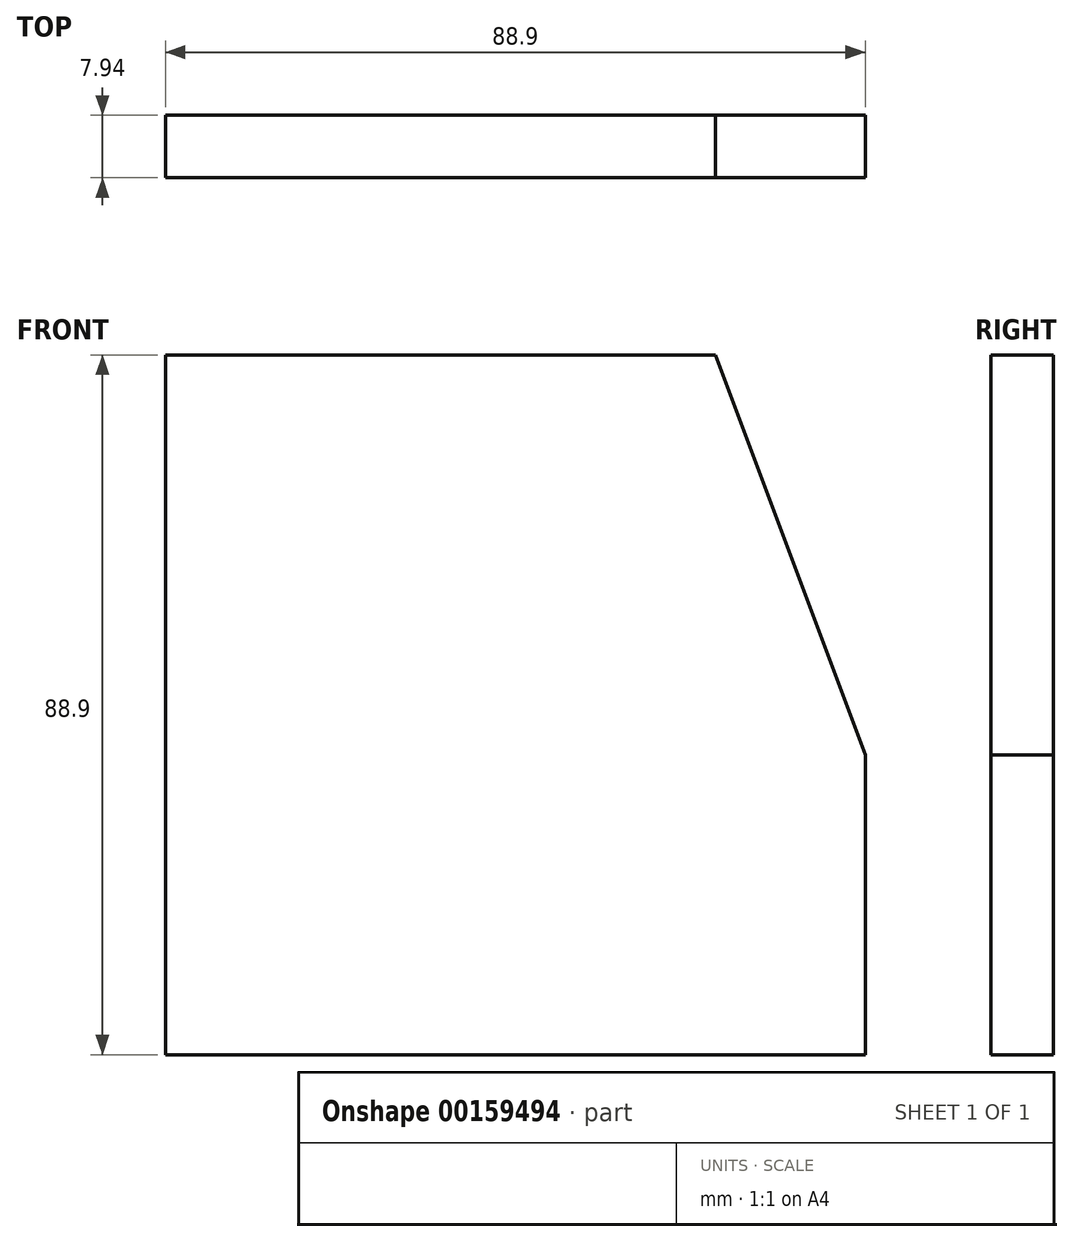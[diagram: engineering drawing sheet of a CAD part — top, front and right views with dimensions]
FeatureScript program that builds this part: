
annotation { "Feature Type Name" : "Feature", "Feature Type Description" : "" }
export const myFeature = defineFeature(function(context is Context, id is Id, definition is map)
    precondition{}
    {
        {
            var Q0;
            Q0=qCreatedBy(makeId("Front.planeOp"),FACE);
            var sketch = newSketch(context, id + "F0", { "sketchPlane" : qUnion([Q0])});
            skLineSegment(sketch, "E0.bottom", {"start": v(-78.75, 134.89) * mm, "end": v(-8.9, 134.89) * mm});
            skLineSegment(sketch, "E0.top", {"start": v(-78.75, 45.99) * mm, "end": v(10.15, 45.99) * mm});
            skLineSegment(sketch, "E0.left", {"start": v(-78.75, 134.89) * mm, "end": v(-78.75, 45.99) * mm});
            skLineSegment(sketch, "E0.right", {"start": v(10.15, 84.09) * mm, "end": v(10.15, 45.99) * mm});
            skLineSegment(sketch, "E1", {"start": v(10.15, 84.09) * mm, "end": v(-8.9, 134.89) * mm});
            skSolve(sketch);
        }
        {
            var Q0;
            Q0=makeQuery(id+"F0.imprint","IMPRINT",FACE,{"disambiguationData":[TD([[makeQuery(id+"F0.imprint","IMPRINT",EDGE,{"derivedFrom":sQuery(id+"F0.wireOp",EDGE,"E0.bottom")}),-1.0]])]});
            extrude(context, id + "F1", {"entities" : qUnion([Q0]), "depth" : 7.94 * mm});
        }
    });
